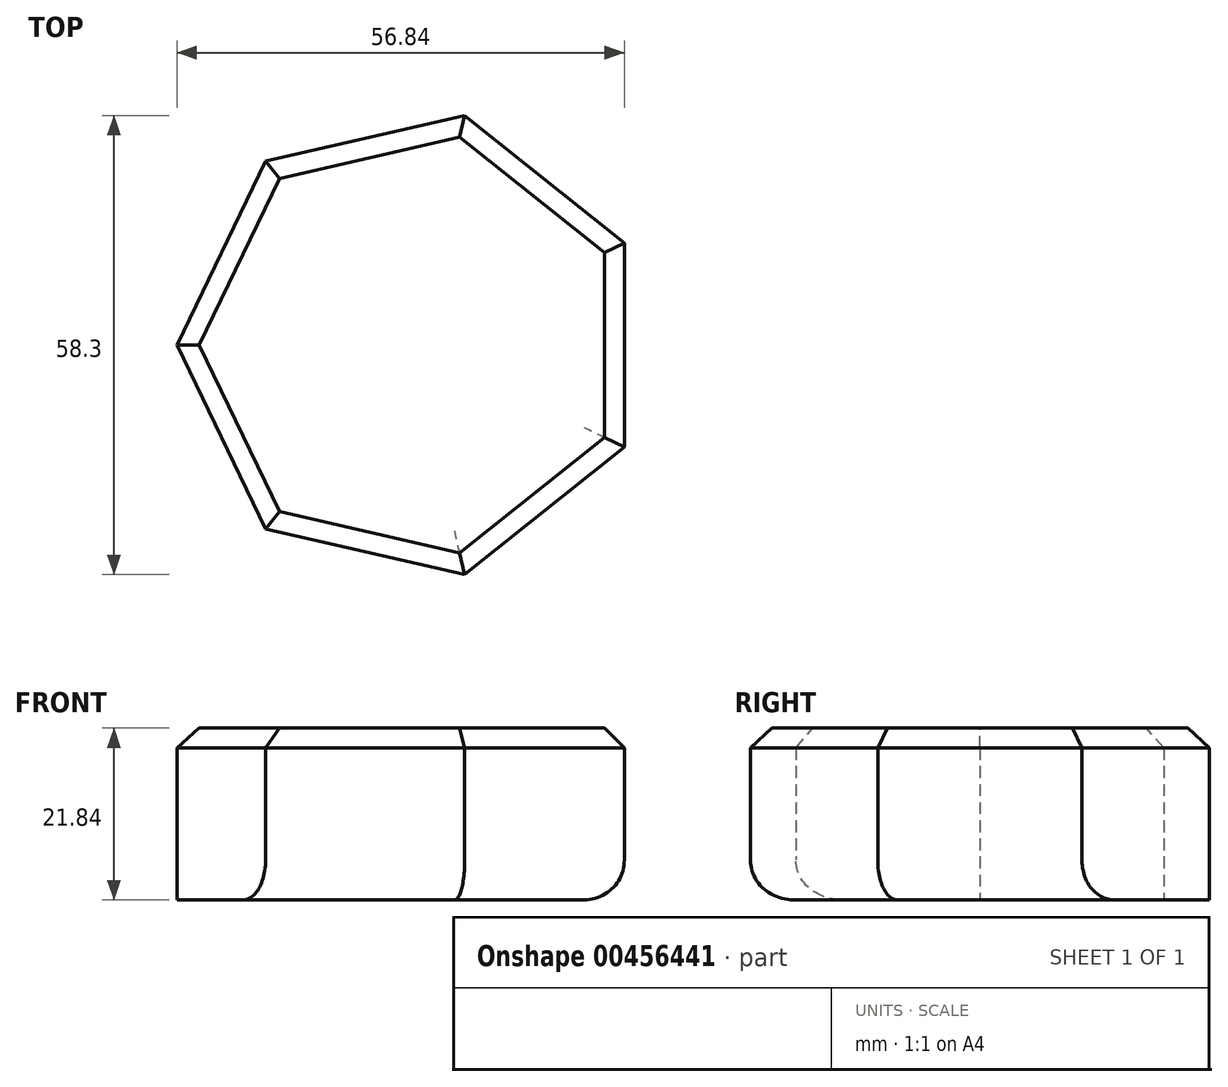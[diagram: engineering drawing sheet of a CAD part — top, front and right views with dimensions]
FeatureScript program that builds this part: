
annotation { "Feature Type Name" : "Feature", "Feature Type Description" : "" }
export const myFeature = defineFeature(function(context is Context, id is Id, definition is map)
    precondition{}
    {
        {
            var Q0;
            Q0=qCreatedBy(makeId("Top.planeOp"),FACE);
            var sketch = newSketch(context, id + "F0", { "sketchPlane" : qUnion([Q0])});
            skCircle(sketch, "E0.cCircle", {"center": v(0, 0) * mm, "radius": 26.94 * mm, "construction": true});
            skLineSegment(sketch, "E0.0", {"start": v(26.94, 12.97) * mm, "end": v(26.94, -12.97) * mm});
            skLineSegment(sketch, "E0.1", {"start": v(26.94, -12.97) * mm, "end": v(6.65, -29.15) * mm});
            skLineSegment(sketch, "E0.2", {"start": v(6.65, -29.15) * mm, "end": v(-18.64, -23.37) * mm});
            skLineSegment(sketch, "E0.3", {"start": v(-18.64, -23.37) * mm, "end": v(-29.9, 0) * mm});
            skLineSegment(sketch, "E0.4", {"start": v(-29.9, 0) * mm, "end": v(-18.64, 23.37) * mm});
            skLineSegment(sketch, "E0.5", {"start": v(-18.64, 23.37) * mm, "end": v(6.65, 29.15) * mm});
            skLineSegment(sketch, "E0.6", {"start": v(6.65, 29.15) * mm, "end": v(26.94, 12.97) * mm});
            skPoint(sketch, "E0.0.midPoint", {"position": v(26.94, 0) * mm});
            skSolve(sketch);
        }
        {
            var Q0;
            Q0=makeQuery(id+"F0.imprint","IMPRINT",FACE,{"disambiguationData":[TD([[makeQuery(id+"F0.imprint","IMPRINT",EDGE,{"derivedFrom":sQuery(id+"F0.wireOp",EDGE,"E0.0")}),-1.0]])]});
            extrude(context, id + "F1", {"entities" : qUnion([Q0]), "depth" : 21.84 * mm});
        }
        {
            var Q0;
            Q0=makeQuery(id+"F1.opExtrude","CAP_EDGE",EDGE,{"disambiguationData":[OSD([sQuery(id+"F0.wireOp",EDGE,"E0.0")])],"isStart":false});
            var Q1;
            Q1=makeQuery(id+"F1.opExtrude","CAP_EDGE",EDGE,{"disambiguationData":[OSD([sQuery(id+"F0.wireOp",EDGE,"E0.1")])],"isStart":false});
            var Q2;
            Q2=makeQuery(id+"F1.opExtrude","CAP_EDGE",EDGE,{"disambiguationData":[OSD([sQuery(id+"F0.wireOp",EDGE,"E0.2")])],"isStart":false});
            var Q3;
            Q3=makeQuery(id+"F1.opExtrude","CAP_EDGE",EDGE,{"disambiguationData":[OSD([sQuery(id+"F0.wireOp",EDGE,"E0.3")])],"isStart":false});
            var Q4;
            Q4=makeQuery(id+"F1.opExtrude","CAP_EDGE",EDGE,{"disambiguationData":[OSD([sQuery(id+"F0.wireOp",EDGE,"E0.4")])],"isStart":false});
            var Q5;
            Q5=makeQuery(id+"F1.opExtrude","CAP_EDGE",EDGE,{"disambiguationData":[OSD([sQuery(id+"F0.wireOp",EDGE,"E0.5")])],"isStart":false});
            var Q6;
            Q6=makeQuery(id+"F1.opExtrude","CAP_EDGE",EDGE,{"disambiguationData":[OSD([sQuery(id+"F0.wireOp",EDGE,"E0.6")])],"isStart":false});
            chamfer(context, id + "F2", {"entities" : qUnion([Q0, Q1, Q2, Q3, Q4, Q5, Q6]), "width" : 2.54 * mm, "tangentPropagation" : true});
        }
        {
            var Q0;
            Q0=makeQuery(id+"F1.opExtrude","CAP_EDGE",EDGE,{"disambiguationData":[OSD([sQuery(id+"F0.wireOp",EDGE,"E0.1")])],"isStart":true});
            var Q1;
            Q1=makeQuery(id+"F1.opExtrude","CAP_EDGE",EDGE,{"disambiguationData":[OSD([sQuery(id+"F0.wireOp",EDGE,"E0.0")])],"isStart":true});
            var Q2;
            Q2=makeQuery(id+"F1.opExtrude","CAP_EDGE",EDGE,{"disambiguationData":[OSD([sQuery(id+"F0.wireOp",EDGE,"E0.2")])],"isStart":true});
            fillet(context, id + "F3", {"entities" : qUnion([Q0, Q1, Q2]), "radius" : 5.08 * mm, "tangentPropagation" : true, "allowEdgeOverflow" : false});
        }
    });
